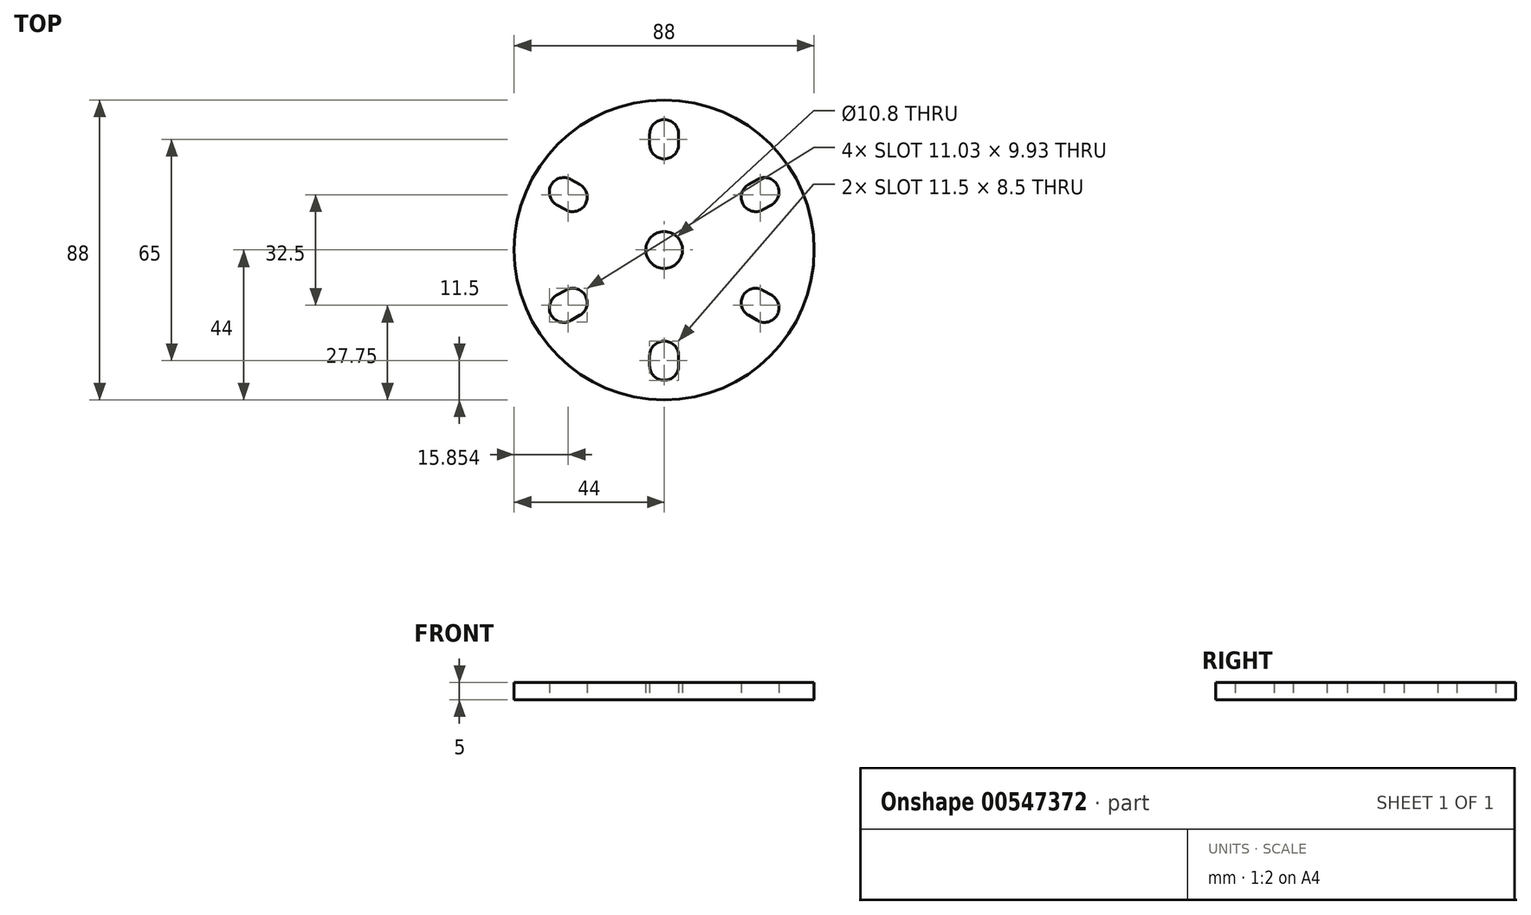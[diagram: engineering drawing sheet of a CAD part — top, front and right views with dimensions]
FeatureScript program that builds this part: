
annotation { "Feature Type Name" : "Feature", "Feature Type Description" : "" }
export const myFeature = defineFeature(function(context is Context, id is Id, definition is map)
    precondition{}
    {
        {
            var Q0;
            Q0=qCreatedBy(makeId("Top.planeOp"),FACE);
            var sketch = newSketch(context, id + "F0", { "sketchPlane" : qUnion([Q0])});
            skCircle(sketch, "E0", {"center": v(0, 0) * mm, "radius": 44 * mm});
            skCircle(sketch, "E1", {"center": v(0, 0) * mm, "radius": 5.4 * mm});
            skCircle(sketch, "E2", {"center": v(0, 0) * mm, "radius": 34 * mm, "construction": true});
            skLineSegment(sketch, "E3.anchor1", {"start": v(0, 0) * mm, "end": v(0, 34) * mm, "construction": true});
            skCircle(sketch, "E4", {"center": v(0, 0) * mm, "radius": 31 * mm, "construction": true});
            skArc(sketch, "E5", {"start": v(4.24, 33.73) * mm, "mid": v(0, 38.25) * mm, "end": v(-4.24, 33.73) * mm});
            skArc(sketch, "E6", {"start": v(-4.25, 31) * mm, "mid": v(0, 26.75) * mm, "end": v(4.25, 31) * mm});
            skLineSegment(sketch, "E7", {"start": v(4.25, 34) * mm, "end": v(4.25, 31) * mm});
            skLineSegment(sketch, "E8", {"start": v(-4.25, 34) * mm, "end": v(-4.25, 31) * mm});
            skArc(sketch, "E9.1.0", {"start": v(-27.1, 20.54) * mm, "mid": v(-33.13, 19.13) * mm, "end": v(-31.34, 13.2) * mm});
            skArc(sketch, "E9.1.1", {"start": v(-28.97, 11.82) * mm, "mid": v(-23.17, 13.37) * mm, "end": v(-24.72, 19.18) * mm});
            skLineSegment(sketch, "E9.1.2", {"start": v(-31.57, 13.32) * mm, "end": v(-28.97, 11.82) * mm});
            skLineSegment(sketch, "E9.1.3", {"start": v(-27.32, 20.68) * mm, "end": v(-24.72, 19.18) * mm});
            skArc(sketch, "E9.2.0", {"start": v(-31.34, -13.2) * mm, "mid": v(-33.13, -19.13) * mm, "end": v(-27.1, -20.54) * mm});
            skArc(sketch, "E9.2.1", {"start": v(-24.72, -19.18) * mm, "mid": v(-23.17, -13.38) * mm, "end": v(-28.97, -11.82) * mm});
            skLineSegment(sketch, "E9.2.2", {"start": v(-27.32, -20.68) * mm, "end": v(-24.72, -19.18) * mm});
            skLineSegment(sketch, "E9.2.3", {"start": v(-31.57, -13.32) * mm, "end": v(-28.97, -11.82) * mm});
            skArc(sketch, "E9.3.0", {"start": v(-4.24, -33.73) * mm, "mid": v(0, -38.25) * mm, "end": v(4.24, -33.73) * mm});
            skArc(sketch, "E9.3.1", {"start": v(4.25, -31) * mm, "mid": v(0, -26.75) * mm, "end": v(-4.25, -31) * mm});
            skLineSegment(sketch, "E9.3.2", {"start": v(4.25, -34) * mm, "end": v(4.25, -31) * mm});
            skLineSegment(sketch, "E9.3.3", {"start": v(-4.25, -34) * mm, "end": v(-4.25, -31) * mm});
            skArc(sketch, "E9.4.0", {"start": v(27.1, -20.54) * mm, "mid": v(33.13, -19.13) * mm, "end": v(31.34, -13.2) * mm});
            skArc(sketch, "E9.4.1", {"start": v(28.97, -11.82) * mm, "mid": v(23.17, -13.38) * mm, "end": v(24.72, -19.18) * mm});
            skLineSegment(sketch, "E9.4.2", {"start": v(31.57, -13.32) * mm, "end": v(28.97, -11.82) * mm});
            skLineSegment(sketch, "E9.4.3", {"start": v(27.32, -20.68) * mm, "end": v(24.72, -19.18) * mm});
            skArc(sketch, "E9.5.0", {"start": v(31.34, 13.2) * mm, "mid": v(33.13, 19.13) * mm, "end": v(27.1, 20.54) * mm});
            skArc(sketch, "E9.5.1", {"start": v(24.72, 19.18) * mm, "mid": v(23.17, 13.38) * mm, "end": v(28.97, 11.82) * mm});
            skLineSegment(sketch, "E9.5.2", {"start": v(27.32, 20.68) * mm, "end": v(24.72, 19.18) * mm});
            skLineSegment(sketch, "E9.5.3", {"start": v(31.57, 13.32) * mm, "end": v(28.97, 11.82) * mm});
            skSolve(sketch);
        }
        {
            var Q0;
            Q0=makeQuery(id+"F0.imprint","IMPRINT",FACE,{"disambiguationData":[TD([[makeQuery(id+"F0.imprint","IMPRINT",EDGE,{"derivedFrom":sQuery(id+"F0.wireOp",EDGE,"E0")}),1.0]])]});
            var Q1;
            Q1 = qConstructionFilter(qBodyType(qCreatedBy(id + "F0" ,EDGE), BodyType.WIRE), ConstructionObject.NO);
            extrude(context, id + "F1", {"entities" : qUnion([Q0]), "surfaceEntities" : qUnion([Q1]), "depth" : 5 * mm, "offsetDistance" : 25 * mm});
        }
    });
